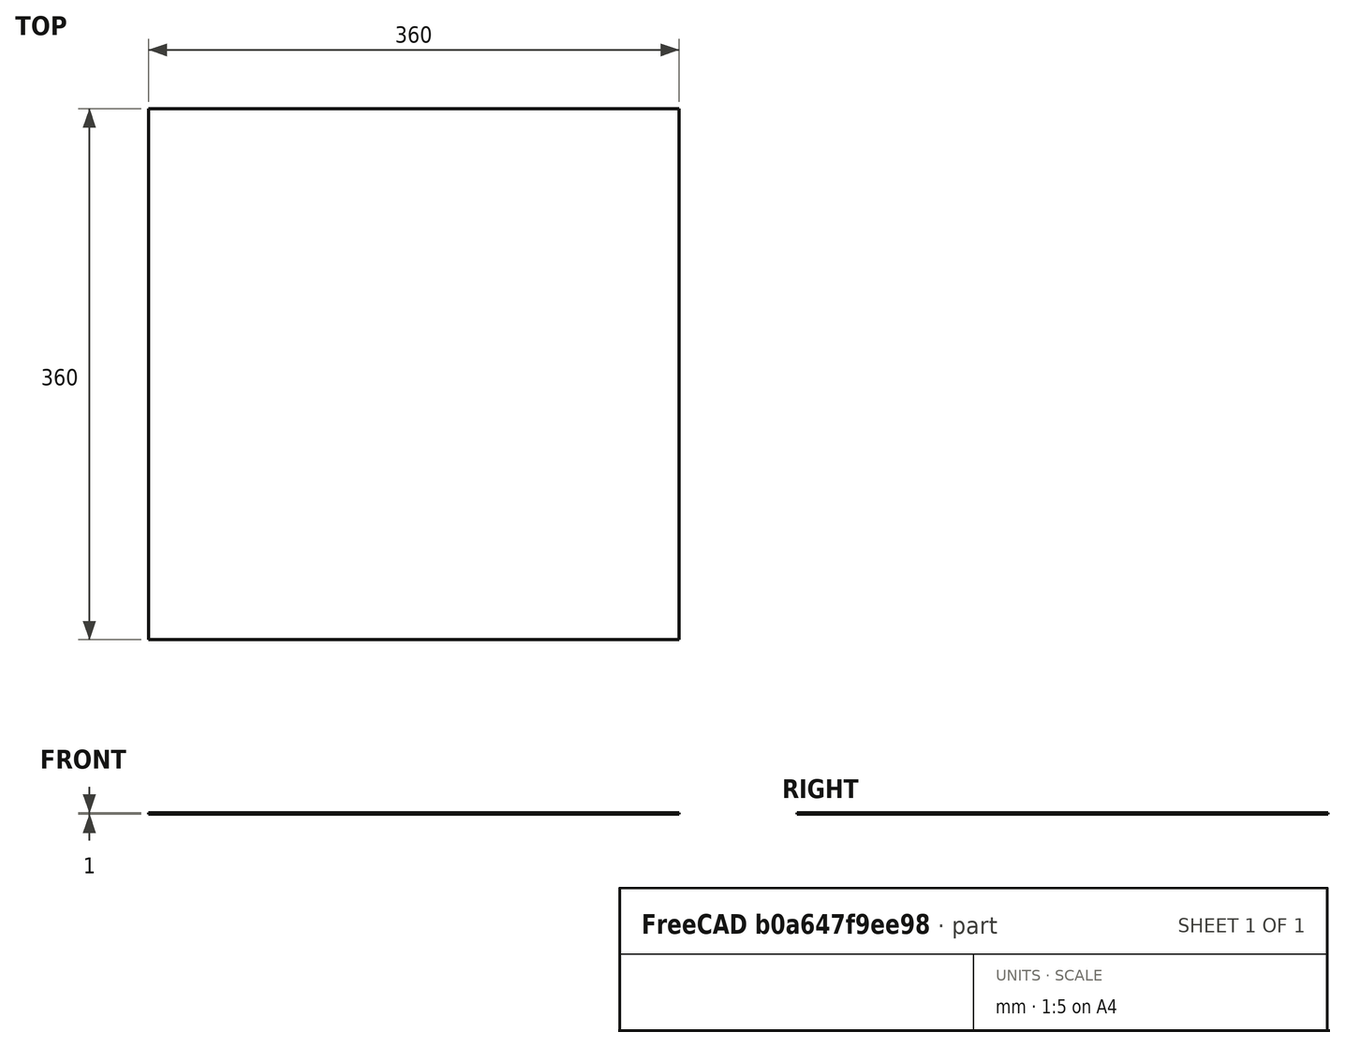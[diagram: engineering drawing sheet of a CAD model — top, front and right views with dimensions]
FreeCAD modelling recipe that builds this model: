
FCSTD DOCUMENT  (FreeCAD 0.21R33675 (Git))
Label: parabolic_simulation
License: All rights reserved
LicenseURL: http://en.wikipedia.org/wiki/All_rights_reserved
objects: Part::FeaturePython×5, App::Link×3, Part::Box×2, Spreadsheet::Sheet×1
note: 7 computed .brp shape members not serialized (recipe doc carries the construction recipe); baked Part::Feature solids carry a one-line shape summary decoded from their .brp
EXTERNAL_REF file=../../templates/tem_octagon.FCStd obj=Compound017
EXTERNAL_REF file=parabolic_screwmount.FCStd obj=Cut
EXTERNAL_REF file=parabolic_base.FCStd obj=Spreadsheet
EXTERNAL_REF file=../../sampleholder/temholder2.FCStd obj=Fusion005

FEATURE [App::Link] Link  label="TemOctagon"
  LinkedObject = -> <external ../../templates/tem_octagon.FCStd>#Compound017
FEATURE [App::Link] Link001  label="ParabolicMirrorWithScrewmount"
  LinkedObject = -> <external parabolic_screwmount.FCStd>#Cut
  expr: .Placement.Base.x = <<SimulationProperties>>.mirror_offset_x
FEATURE [Part::Box] Box  label="LowerAbsorber"
  AttacherType = Attacher::AttachEngine3D
  Height = 1
  Length = 360
  Placement = pos=(-180,-180,-41) rot=(0,0,1;0rad)
  Width = 360
FEATURE [Part::Box] Box001  label="UpperAbsorber"
  AttacherType = Attacher::AttachEngine3D
  Height = 1
  Length = 360
  Placement = pos=(-180,-180,40) rot=(0,0,1;0rad)
  Width = 360
FEATURE [Part::FeaturePython] Absorber  label="AbsorbLowerAndUpperBoundary"  # WARN: FeaturePython — macro-defined, semantics opaque (R4)
  Base = -> [Box001,Box]
  HitCoordsFromBeam = (34) [(0,0,40),(29.0617,0,40),(14.5309,25.1682,40),(-14.5309,25.1682,40),(-29.0617,3.55903e-15,40),(-14.5309,-25.1682,40),(14.5309,-25.1682,40),+27 more]
  HitCoordsFromBeamSample = (25) [(0,0,40),(-16.8699,9.73985,40),(-19.4797,2.38557e-15,40),(-16.8699,-9.73985,40),(-24.7109,20.7349,40),(-30.3124,11.0328,40),(-32.2578,3.95044e-15,40),+18 more]
  HitsFromBeam = 34
  HitsFromBeamSample = 25
  OpticalType = 1
FEATURE [Part::FeaturePython] Absorber001  label="AbsorbTemOctagon"  # WARN: FeaturePython — macro-defined, semantics opaque (R4)
  Base = -> [Link]
  HitsFromBeamSample = 0
  OpticalType = 1
FEATURE [Spreadsheet::Sheet] Spreadsheet  label="SimulationProperties"
  cells = A1='Configuration; D1='Imported from parabolic_base; G1='Calculated properties; A2='Out of focus: z; B2(outoffocus_z)=0; C2='Puts the sample out of focus by this distance; D2='Z Positon correction / Offset (downwards) ; E2(focus_offset_z)==parabolic_base#<<MirrorParameters>>.zpos_correction; G2='Sample z; H2(sample_z)==outoffocus_z - focus_offset_z; I2='The sample position; A3='Out of focus: x; B3(outoffocus_x)=0; C3='Puts the sample out of focus by this distance; G3='Sample x; H3(sample_x)==outoffocus_x; I3='The sample position; A4='Out of focus: y; B4(outoffocus_y)=0; C4='Puts the sample out of focus by this distance; G4='Sample y; H4(sample_y)==outoffocus_y; I4='The sample position; A5='Cone angle; B5(sample_cone_angle)=180; C5='The emission angle (180 deg only towards the top, 360 degree spherical); G5='Total number of rays; H5(simulation_n_rays)==raysperaxis * raysperaxis; A6='Rays per axis; B6(raysperaxis)=128; C6='Number of rays per axis; A7='Mirror position (X); B7(mirror_offset_x)=0; C7='Move the mirror this distance _away from the holder_ (negative value: Towards the holder)
FEATURE [Part::FeaturePython] Beam  label="BeamSample"  # WARN: FeaturePython — macro-defined, semantics opaque (R4)
  BeamDistance = 0.05
  BeamNrColumns = 128
  BeamNrRows = 128
  ConeAngle = 180
  HideFirstPart = false
  MaxNrReflections = 1000
  MaxRayLength = 1000000
  Order = 0
  Placement = pos=(0,0,-0.45) rot=(0,0,1;0rad)
  Power = true
  Spherical = true
  Wavelength = 400
  expr: .Placement.Base.x = <<SimulationProperties>>.sample_x
  expr: .Placement.Base.y = <<SimulationProperties>>.sample_y
  expr: .Placement.Base.z = <<SimulationProperties>>.sample_z
  expr: BeamNrColumns = <<SimulationProperties>>.raysperaxis
  expr: BeamNrRows = <<SimulationProperties>>.raysperaxis
  expr: ConeAngle = <<SimulationProperties>>.sample_cone_angle
FEATURE [Part::FeaturePython] Absorber002  label="Mirror"  # WARN: FeaturePython — macro-defined, semantics opaque (R4)
  Base = -> [Link001]
  HitsFromBeamSample = 60
  OpticalType = 0
FEATURE [App::Link] Link002  label="TemHolder"
  LinkPlacement = pos=(35.2,0,-0.48) rot=(0,1,0;-1.5708rad)
  LinkedObject = -> <external ../../sampleholder/temholder2.FCStd>#Fusion005
  Placement = pos=(35.2,0,-0.48) rot=(0,1,0;-1.5708rad)
  expr: .Placement.Base.z = -<<parabolic_base>>#<<MirrorParameters>>.step_height - 0.3
FEATURE [Part::FeaturePython] Absorber003  label="AbsorbHolder"  # WARN: FeaturePython — macro-defined, semantics opaque (R4)
  Base = -> [Link002]
  HitCoordsFromBeamSample = (77) [(1.695,0,-0.541717),(1.62634,0.477537,-0.541717),(1.42592,0.916386,-0.541717),(1.10999,1.281,-0.541717),(1.10999,-1.281,-0.541717),+72 more]
  HitsFromBeamSample = 77
  OpticalType = 1

RESOLVED EXTERNAL PARTS (link-assembly join: the EXTERNAL_REF files above that resolve inside this repo's crawl, each included once):
---- part ../../sampleholder/temholder2.FCStd = doc fcstd_919bdca02343 ----
FCSTD DOCUMENT  (FreeCAD 0.21R33675 (Git))
Label: temholder2
License: All rights reserved
LicenseURL: http://en.wikipedia.org/wiki/All_rights_reserved
objects: TechDraw::DrawViewDimension×22, Part::Cylinder×10, TechDraw::DrawProjGroupItem×10, Part::Cut×8, Part::Box×7, Part::MultiFuse×6, TechDraw::DrawSVGTemplate×2, TechDraw::DrawProjGroup×2, TechDraw::DrawPage×2, Part::MultiCommon×1
note: 32 computed .brp shape members not serialized (recipe doc carries the construction recipe); baked Part::Feature solids carry a one-line shape summary decoded from their .brp

FEATURE [Part::Cylinder] Cylinder  label="Zylinder"
  Angle = 360
  AttacherType = Attacher::AttachEngine3D
  FirstAngle = 0
  Height = 21.5
  Placement = pos=(0,0,-0.5) rot=(0,0,1;0rad)
  Radius = 2.2
  SecondAngle = 0
FEATURE [Part::Cylinder] Cylinder001  label="Zylinder001"
  Angle = 360
  AttacherType = Attacher::AttachEngine3D
  FirstAngle = 0
  Height = 18
  Placement = pos=(0,0,5) rot=(0,0,1;0rad)
  Radius = 2.5
  SecondAngle = 0
FEATURE [Part::Cylinder] Cylinder002  label="Zylinder002"
  Angle = 360
  AttacherType = Attacher::AttachEngine3D
  FirstAngle = 0
  Height = 6.2
  Placement = pos=(-3.25,0,2.95) rot=(0,1,0;1.5708rad)
  Radius = 0.75
  SecondAngle = 0
FEATURE [Part::MultiFuse] Fusion
  Shapes = -> [Cylinder,Cylinder001]
FEATURE [Part::Cut] Cut
  Base = -> Fusion
  Tool = -> Cylinder002
FEATURE [Part::Box] Box  label="Würfel"
  AttacherType = Attacher::AttachEngine3D
  Height = 27.9
  Length = 2
  Placement = pos=(-1,-5,21) rot=(0,0,1;0rad)
  Width = 10
FEATURE [Part::Cylinder] Cylinder003  label="BeamHole"
  Angle = 360
  AttacherType = Attacher::AttachEngine3D
  FirstAngle = 0
  Height = 2
  Placement = pos=(-1,0,35.2) rot=(0,1,0;1.5708rad)
  Radius = 1.1
  SecondAngle = 0
FEATURE [Part::Cylinder] Cylinder004  label="Zylinder004"
  Angle = 360
  AttacherType = Attacher::AttachEngine3D
  FirstAngle = 0
  Height = 27.4
  Placement = pos=(0,0,21.5) rot=(0,0,1;0rad)
  Radius = 3
  SecondAngle = 0
FEATURE [Part::MultiCommon] Common
  Shapes = -> [Cylinder004,Box]
FEATURE [Part::Cut] Cut001
  Base = -> Common
  Tool = -> Cylinder003
FEATURE [Part::Cylinder] Cylinder005  label="Zylinder005"
  Angle = 360
  AttacherType = Attacher::AttachEngine3D
  FirstAngle = 0
  Height = 5.5
  Placement = pos=(0,0,-0.5) rot=(0,0,1;0rad)
  Radius = 1
  SecondAngle = 0
FEATURE [Part::Cut] Cut002
  Base = -> Cut
  Tool = -> Cylinder005
FEATURE [Part::Cylinder] Cylinder006  label="ProbeHole"
  Angle = 360
  AttacherType = Attacher::AttachEngine3D
  FirstAngle = 0
  Height = 20
  Placement = pos=(-4,0,35.2) rot=(0,1,0;1.5708rad)
  Radius = 1.695
  SecondAngle = 0
FEATURE [Part::Cut] Cut003
  Base = -> Cut001
  Tool = -> Cylinder006
FEATURE [Part::Box] Box001  label="Würfel001"
  AttacherType = Attacher::AttachEngine3D
  Height = 27
  Length = 10
  Placement = pos=(1,-2.57,21) rot=(0,0,1;0rad)
  Width = 5.5
FEATURE [Part::Cut] Cut004
  Base = -> Cut003
  Tool = -> Box001
FEATURE [Part::MultiFuse] Fusion001
  Shapes = -> [Cut002,Cut004]
FEATURE [Part::Box] Box002  label="Würfel002"
  AttacherType = Attacher::AttachEngine3D
  Height = 1.5
  Length = 1
  Placement = pos=(-0.5,-3.2,21.5) rot=(0,0,1;0rad)
  Width = 6.4
FEATURE [Part::Box] Box003  label="Würfel003"
  AttacherType = Attacher::AttachEngine3D
  Height = 26
  Length = 10
  Placement = pos=(0.5,-2.19,23) rot=(0,0,1;0rad)
  Width = 4.37
FEATURE [Part::Box] Box004  label="Würfel004"
  AttacherType = Attacher::AttachEngine3D
  Height = 26
  Length = 10
  Placement = pos=(-10.5,-2.19,23) rot=(0,0,1;0rad)
  Width = 4.37
FEATURE [Part::MultiFuse] Fusion002  label="MirrorGrooves"
  Shapes = -> [Box004,Box003]
FEATURE [Part::Cut] Cut005
  Base = -> Fusion001
  Tool = -> Fusion002
FEATURE [Part::Cylinder] Cylinder007  label="M1_6__Thread1"
  Angle = 360
  AttacherType = Attacher::AttachEngine3D
  FirstAngle = 0
  Height = 50
  Placement = pos=(-4,0,31.405) rot=(0,1,0;1.5708rad)
  Radius = 0.59
  SecondAngle = 0
FEATURE [Part::Cylinder] Cylinder008  label="M1_6__Thread2"
  Angle = 360
  AttacherType = Attacher::AttachEngine3D
  FirstAngle = 0
  Height = 50
  Placement = pos=(-4,0,29.41) rot=(0,1,0;1.5708rad)
  Radius = 0.59
  SecondAngle = 0
FEATURE [Part::Box] Box005  label="Würfel005"
  AttacherType = Attacher::AttachEngine3D
  Height = 12
  Length = 10
  Placement = pos=(0.25,-2.19,36.77) rot=(0,0,1;0rad)
  Width = 4.37
FEATURE [Part::Box] Box006  label="Würfel006"
  AttacherType = Attacher::AttachEngine3D
  Height = 12
  Length = 10
  Placement = pos=(-10.25,-2.19,36.77) rot=(0,0,1;0rad)
  Width = 4.37
FEATURE [Part::MultiFuse] Fusion004
  Placement = pos=(0,0,1) rot=(0,0,1;0rad)
  Shapes = -> [Box005,Box006]
FEATURE [TechDraw::DrawSVGTemplate] Template
  EditableTexts = Designed_by_Name=Thomas Spielauer; Drawing_number=001; FC-Date=2023-05-22; FC-SC=2:1; FC-SH=2/2; FC-Title=TEM Mirror Holder; Subtitle=Version 2023-05-22
  Height = 210
  Orientation = 1
  Width = 297
FEATURE [TechDraw::DrawSVGTemplate] Template001
  EditableTexts = Designed_by_Name=Thomas Spielauer; Drawing_number=001; FC-Date=2023-05-22; FC-SC=3:2; FC-SH=2/2; FC-Title=TEM Mirror Holder; Subtitle=Version 2023-05-22
  Height = 210
  Orientation = 1
  Width = 297
FEATURE [Part::Cylinder] Cylinder009  label="M1_6__Thread3"
  Angle = 360
  AttacherType = Attacher::AttachEngine3D
  FirstAngle = 0
  Height = 50
  Placement = pos=(-4,0,27.41) rot=(0,1,0;1.5708rad)
  Radius = 0.59
  SecondAngle = 0
FEATURE [Part::MultiFuse] Fusion003  label="MirrorMountingHoles"
  Shapes = -> [Cylinder007,Cylinder008,Cylinder009]
FEATURE [Part::Cut] Cut006
  Base = -> Cut005
  Tool = -> Fusion003
FEATURE [Part::Cut] Cut007
  Base = -> Cut006
  Tool = -> Fusion004
FEATURE [Part::MultiFuse] Fusion005
  Shapes = -> [Cut007,Box002]
FEATURE [TechDraw::DrawProjGroupItem] ProjItem  label="Front"
  CoarseView = false
  Direction = (1,0,0)
  Focus = 100
  HardHidden = false
  IsoCount = 0
  IsoHidden = false
  IsoVisible = false
  LockPosition = true
  Perspective = false
  Rotation = 0
  RotationVector = (0,1,0)
  Scale = 2
  ScaleType = 2
  ScrubCount = 0
  SeamHidden = false
  SeamVisible = true
  SmoothHidden = false
  SmoothVisible = true
  Source = -> [Fusion005]
  Type = 0
  X = 0
  XDirection = (0,-2e-16,-1)
  Y = 0
FEATURE [TechDraw::DrawProjGroupItem] ProjItem001  label="Left"
  CoarseView = false
  Direction = (1e-16,2e-16,1)
  Focus = 100
  HardHidden = false
  IsoCount = 0
  IsoHidden = false
  IsoVisible = false
  LockPosition = false
  Perspective = false
  Rotation = 0
  RotationVector = (1,0,0)
  Scale = 2
  ScaleType = 2
  ScrubCount = 0
  SeamHidden = false
  SeamVisible = true
  SmoothHidden = false
  SmoothVisible = true
  Source = -> [Fusion005]
  Type = 1
  X = 54.4
  XDirection = (1,0,-1e-16)
  Y = 0
FEATURE [TechDraw::DrawProjGroupItem] ProjItem003  label="Right"
  CoarseView = false
  Direction = (1e-16,-2e-16,-1)
  Focus = 100
  HardHidden = false
  IsoCount = 0
  IsoHidden = false
  IsoVisible = false
  LockPosition = false
  Perspective = false
  Rotation = 0
  RotationVector = (1,0,0)
  Scale = 2
  ScaleType = 2
  ScrubCount = 0
  SeamHidden = false
  SeamVisible = true
  SmoothHidden = false
  SmoothVisible = true
  Source = -> [Fusion005]
  Type = 2
  X = -54.4
  XDirection = (-1,0,-1e-16)
  Y = 0
FEATURE [TechDraw::DrawProjGroupItem] ProjItem004  label="Bottom"
  CoarseView = false
  Direction = (0,-1,2e-16)
  Focus = 100
  HardHidden = false
  IsoCount = 0
  IsoHidden = false
  IsoVisible = false
  LockPosition = false
  Perspective = false
  Rotation = 0
  RotationVector = (1,0,0)
  ScaleType = 2
  ScrubCount = 0
  SeamHidden = false
  SeamVisible = true
  SmoothHidden = false
  SmoothVisible = true
  Source = -> [Fusion005]
  Type = 5
  X = 0
  XDirection = (0,-2e-16,-1)
  Y = 41.4
FEATURE [TechDraw::DrawProjGroup] ProjGroup
  Anchor = -> ProjItem
  AutoDistribute = true
  LockPosition = false
  ProjectionType = 0
  Rotation = 0
  Scale = 2
  ScaleType = 1
  Source = -> [Fusion005]
  Views = -> [ProjItem,ProjItem001,ProjItem003,ProjItem004]
  X = 148.5
  Y = 105
  spacingX = 0
  spacingY = 30
FEATURE [TechDraw::DrawViewDimension] Dimension
  AngleOverride = false
  Arbitrary = false
  ArbitraryTolerances = false
  EqualTolerance = true
  ExtensionAngle = 0
  FormatSpec = %.2w
  FormatSpecOverTolerance = %+.2w
  FormatSpecUnderTolerance = %+.2w
  Inverted = false
  LineAngle = 0
  LockPosition = false
  MeasureType = 1
  OverTolerance = 0
  References2D = -> [ProjItem004]
  Rotation = 0
  ScaleType = 0
  TheoreticalExact = false
  Type = 0
  UnderTolerance = 0
  X = -0.570385
  Y = 36.7256
FEATURE [TechDraw::DrawViewDimension] Dimension001
  AngleOverride = false
  Arbitrary = false
  ArbitraryTolerances = false
  EqualTolerance = true
  ExtensionAngle = 0
  FormatSpec = %.2w
  FormatSpecOverTolerance = %+.2w
  FormatSpecUnderTolerance = %+.2w
  Inverted = false
  LineAngle = 0
  LockPosition = false
  MeasureType = 1
  OverTolerance = 0
  References2D = -> [ProjItem004]
  Rotation = 0
  ScaleType = 0
  TheoreticalExact = false
  Type = 0
  UnderTolerance = 0
  X = 43.2488
  Y = 27.3992
FEATURE [TechDraw::DrawViewDimension] Dimension002
  AngleOverride = false
  Arbitrary = false
  ArbitraryTolerances = false
  EqualTolerance = true
  ExtensionAngle = 0
  FormatSpec = %.2w
  FormatSpecOverTolerance = %+.2w
  FormatSpecUnderTolerance = %+.2w
  Inverted = false
  LineAngle = 0
  LockPosition = false
  MeasureType = 1
  OverTolerance = 0
  References2D = -> [ProjItem004]
  Rotation = 0
  ScaleType = 0
  TheoreticalExact = false
  Type = 0
  UnderTolerance = 0
  X = 20.4028
  Y = 27.4177
FEATURE [TechDraw::DrawViewDimension] Dimension003
  AngleOverride = false
  Arbitrary = false
  ArbitraryTolerances = false
  EqualTolerance = true
  ExtensionAngle = 0
  FormatSpec = %.2w
  FormatSpecOverTolerance = %+.2w
  FormatSpecUnderTolerance = %+.2w
  Inverted = false
  LineAngle = 0
  LockPosition = false
  MeasureType = 1
  OverTolerance = 0
  References2D = -> [ProjItem004]
  Rotation = 0
  ScaleType = 0
  TheoreticalExact = false
  Type = 0
  UnderTolerance = 0
  X = -20.5047
  Y = 16.0274
FEATURE [TechDraw::DrawViewDimension] Dimension004
  AngleOverride = false
  Arbitrary = false
  ArbitraryTolerances = false
  EqualTolerance = true
  ExtensionAngle = 0
  FormatSpec = %.2w
  FormatSpecOverTolerance = %+.2w
  FormatSpecUnderTolerance = %+.2w
  Inverted = false
  LineAngle = 0
  LockPosition = false
  MeasureType = 1
  OverTolerance = 0
  References2D = -> [ProjItem004]
  Rotation = 0
  ScaleType = 0
  TheoreticalExact = false
  Type = 0
  UnderTolerance = 0
  X = 8.18137
  Y = 19.112
FEATURE [TechDraw::DrawViewDimension] Dimension005
  AngleOverride = false
  Arbitrary = false
  ArbitraryTolerances = false
  EqualTolerance = true
  ExtensionAngle = 0
  FormatSpec = %.2w
  FormatSpecOverTolerance = %+.2w
  FormatSpecUnderTolerance = %+.2w
  Inverted = false
  LineAngle = 0
  LockPosition = false
  MeasureType = 1
  OverTolerance = 0
  References2D = -> [ProjItem004]
  Rotation = 0
  ScaleType = 0
  TheoreticalExact = false
  Type = 0
  UnderTolerance = 0
  X = 68.2961
  Y = 3.13583
FEATURE [TechDraw::DrawViewDimension] Dimension006
  AngleOverride = false
  Arbitrary = false
  ArbitraryTolerances = false
  EqualTolerance = true
  ExtensionAngle = 0
  FormatSpec = %.2w
  FormatSpecOverTolerance = %+.2w
  FormatSpecUnderTolerance = %+.2w
  Inverted = false
  LineAngle = 0
  LockPosition = false
  MeasureType = 1
  OverTolerance = 0
  References2D = -> [ProjItem004]
  Rotation = 0
  ScaleType = 0
  TheoreticalExact = false
  Type = 0
  UnderTolerance = 0
  X = 78.1774
  Y = 10.4092
FEATURE [TechDraw::DrawViewDimension] Dimension007
  AngleOverride = false
  Arbitrary = false
  ArbitraryTolerances = false
  EqualTolerance = true
  ExtensionAngle = 0
  FormatSpec = %.2w
  FormatSpecOverTolerance = %+.2w
  FormatSpecUnderTolerance = %+.2w
  Inverted = false
  LineAngle = 0
  LockPosition = false
  MeasureType = 1
  OverTolerance = 0
  References2D = -> [ProjItem004]
  Rotation = 0
  ScaleType = 0
  TheoreticalExact = false
  Type = 0
  UnderTolerance = 0
  X = -59.0159
  Y = 3.08043
FEATURE [TechDraw::DrawViewDimension] Dimension008
  AngleOverride = false
  Arbitrary = false
  ArbitraryTolerances = false
  EqualTolerance = true
  ExtensionAngle = 0
  FormatSpec = %.2w
  FormatSpecOverTolerance = %+.2w
  FormatSpecUnderTolerance = %+.2w
  Inverted = false
  LineAngle = 0
  LockPosition = false
  MeasureType = 1
  OverTolerance = 0
  References2D = -> [ProjItem004]
  Rotation = 0
  ScaleType = 0
  TheoreticalExact = false
  Type = 0
  UnderTolerance = 0
  X = 17.8117
  Y = -5.66689
FEATURE [TechDraw::DrawViewDimension] Dimension010
  AngleOverride = false
  Arbitrary = false
  ArbitraryTolerances = false
  EqualTolerance = true
  ExtensionAngle = 0
  FormatSpec = %.2w
  FormatSpecOverTolerance = %+.2w
  FormatSpecUnderTolerance = %+.2w
  Inverted = false
  LineAngle = 0
  LockPosition = false
  MeasureType = 1
  OverTolerance = 0
  References2D = -> [ProjItem]
  Rotation = 0
  ScaleType = 0
  TheoreticalExact = false
  Type = 0
  UnderTolerance = 0
  X = -80.5776
  Y = 1.58527
FEATURE [TechDraw::DrawViewDimension] Dimension011
  AngleOverride = false
  Arbitrary = false
  ArbitraryTolerances = false
  EqualTolerance = true
  ExtensionAngle = 0
  FormatSpec = %.2w
  FormatSpecOverTolerance = %+.2w
  FormatSpecUnderTolerance = %+.2w
  Inverted = false
  LineAngle = 0
  LockPosition = false
  MeasureType = 1
  OverTolerance = 0
  References2D = -> [ProjItem]
  Rotation = 0
  ScaleType = 0
  TheoreticalExact = false
  Type = 0
  UnderTolerance = 0
  X = -69.6018
  Y = 1.50597
FEATURE [TechDraw::DrawViewDimension] Dimension012
  AngleOverride = false
  Arbitrary = false
  ArbitraryTolerances = false
  EqualTolerance = true
  ExtensionAngle = 0
  FormatSpec = %.2w
  FormatSpecOverTolerance = %+.2w
  FormatSpecUnderTolerance = %+.2w
  Inverted = false
  LineAngle = 0
  LockPosition = false
  MeasureType = 1
  OverTolerance = 0
  References2D = -> [ProjItem]
  Rotation = 0
  ScaleType = 0
  TheoreticalExact = false
  Type = 0
  UnderTolerance = 0
  X = 80.5725
  Y = 4.77787
FEATURE [TechDraw::DrawViewDimension] Dimension013
  AngleOverride = false
  Arbitrary = false
  ArbitraryTolerances = false
  EqualTolerance = true
  ExtensionAngle = 0
  FormatSpec = %.2w
  FormatSpecOverTolerance = %+.2w
  FormatSpecUnderTolerance = %+.2w
  Inverted = false
  LineAngle = 0
  LockPosition = false
  MeasureType = 1
  OverTolerance = 0
  References2D = -> [ProjItem]
  Rotation = 0
  ScaleType = 0
  TheoreticalExact = false
  Type = 0
  UnderTolerance = 0
  X = 58.3431
  Y = 1.78358
FEATURE [TechDraw::DrawViewDimension] Dimension014
  AngleOverride = false
  Arbitrary = false
  ArbitraryTolerances = false
  EqualTolerance = true
  ExtensionAngle = 0
  FormatSpec = %.2w
  FormatSpecOverTolerance = %+.2w
  FormatSpecUnderTolerance = %+.2w
  Inverted = false
  LineAngle = 0
  LockPosition = false
  MeasureType = 1
  OverTolerance = 0
  References2D = -> [ProjItem]
  Rotation = 0
  ScaleType = 0
  TheoreticalExact = false
  Type = 0
  UnderTolerance = 0
  X = 69.2835
  Y = 2.85821
FEATURE [TechDraw::DrawViewDimension] Dimension015
  AngleOverride = false
  Arbitrary = false
  ArbitraryTolerances = false
  EqualTolerance = true
  ExtensionAngle = 0
  FormatSpec = ⌀%.2w
  FormatSpecOverTolerance = %+.2w
  FormatSpecUnderTolerance = %+.2w
  Inverted = false
  LineAngle = 0
  LockPosition = false
  MeasureType = 1
  OverTolerance = 0
  References2D = -> [ProjItem]
  Rotation = 0
  ScaleType = 0
  TheoreticalExact = false
  Type = 5
  UnderTolerance = 0
  X = -17.8818
  Y = -30.5126
FEATURE [TechDraw::DrawViewDimension] Dimension016
  AngleOverride = false
  Arbitrary = false
  ArbitraryTolerances = false
  EqualTolerance = true
  ExtensionAngle = 0
  FormatSpec = ⌀%.2w
  FormatSpecOverTolerance = %+.2w
  FormatSpecUnderTolerance = %+.2w
  Inverted = false
  LineAngle = 0
  LockPosition = false
  MeasureType = 1
  OverTolerance = 0
  References2D = -> [ProjItem]
  Rotation = 0
  ScaleType = 0
  TheoreticalExact = false
  Type = 5
  UnderTolerance = 0
  X = -6.5506
  Y = -20.9661
FEATURE [TechDraw::DrawViewDimension] Dimension017
  AngleOverride = false
  Arbitrary = false
  ArbitraryTolerances = false
  EqualTolerance = true
  ExtensionAngle = 0
  FormatSpec = ⌀%.2w
  FormatSpecOverTolerance = %+.2w
  FormatSpecUnderTolerance = %+.2w
  Inverted = false
  LineAngle = 0
  LockPosition = false
  MeasureType = 1
  OverTolerance = 0
  References2D = -> [ProjItem]
  Rotation = 0
  ScaleType = 0
  TheoreticalExact = false
  Type = 5
  UnderTolerance = 0
  X = 0
  Y = -20.3856
FEATURE [TechDraw::DrawViewDimension] Dimension018
  AngleOverride = false
  Arbitrary = false
  ArbitraryTolerances = false
  EqualTolerance = true
  ExtensionAngle = 0
  FormatSpec = %.2w
  FormatSpecOverTolerance = %+.2w
  FormatSpecUnderTolerance = %+.2w
  Inverted = false
  LineAngle = 0
  LockPosition = false
  MeasureType = 1
  OverTolerance = 0
  References2D = -> [ProjItem]
  Rotation = 0
  ScaleType = 0
  TheoreticalExact = false
  Type = 0
  UnderTolerance = 0
  X = 37.2627
  Y = -7.40421
FEATURE [TechDraw::DrawViewDimension] Dimension019
  AngleOverride = false
  Arbitrary = false
  ArbitraryTolerances = false
  EqualTolerance = true
  ExtensionAngle = 0
  FormatSpec = %.2w
  FormatSpecOverTolerance = %+.2w
  FormatSpecUnderTolerance = %+.2w
  Inverted = false
  LineAngle = 0
  LockPosition = false
  MeasureType = 1
  OverTolerance = 0
  References2D = -> [ProjItem001]
  Rotation = 0
  ScaleType = 0
  TheoreticalExact = false
  Type = 0
  UnderTolerance = 0
  X = 14.265
  Y = 2.24769
FEATURE [TechDraw::DrawViewDimension] Dimension020
  AngleOverride = false
  Arbitrary = false
  ArbitraryTolerances = false
  EqualTolerance = true
  ExtensionAngle = 0
  FormatSpec = ⌀%.2w
  FormatSpecOverTolerance = %+.2w
  FormatSpecUnderTolerance = %+.2w
  Inverted = false
  LineAngle = 0
  LockPosition = false
  MeasureType = 1
  OverTolerance = 0
  References2D = -> [ProjItem001]
  Rotation = 0
  ScaleType = 0
  TheoreticalExact = false
  Type = 5
  UnderTolerance = 0
  X = -8.46963
  Y = -24.8974
FEATURE [TechDraw::DrawViewDimension] Dimension021
  AngleOverride = false
  Arbitrary = false
  ArbitraryTolerances = false
  EqualTolerance = true
  ExtensionAngle = 0
  FormatSpec = %.2w
  FormatSpecOverTolerance = %+.2w
  FormatSpecUnderTolerance = %+.2w
  Inverted = false
  LineAngle = 0
  LockPosition = false
  MeasureType = 1
  OverTolerance = 0
  References2D = -> [ProjItem003]
  Rotation = 0
  ScaleType = 0
  TheoreticalExact = false
  Type = 0
  UnderTolerance = 0
  X = 0
  Y = 15.8224
FEATURE [TechDraw::DrawViewDimension] Dimension022
  AngleOverride = false
  Arbitrary = false
  ArbitraryTolerances = false
  EqualTolerance = true
  ExtensionAngle = 0
  FormatSpec = %.2w
  FormatSpecOverTolerance = %+.2w
  FormatSpecUnderTolerance = %+.2w
  Inverted = false
  LineAngle = 0
  LockPosition = false
  MeasureType = 1
  OverTolerance = 0
  References2D = -> [ProjItem003]
  Rotation = 0
  ScaleType = 0
  TheoreticalExact = false
  Type = 0
  UnderTolerance = 0
  X = -0.516427
  Y = -17.6903
FEATURE [TechDraw::DrawPage] Page
  KeepUpdated = true
  NextBalloonIndex = 1
  ProjectionType = 0
  Template = -> Template
  Views = -> [ProjGroup,Dimension,Dimension001,Dimension002,Dimension003,Dimension004,Dimension005,Dimension006,Dimension007,Dimension008,Dimension010,Dimension011,Dimension012,Dimension013,Dimension014,Dimension015,Dimension016,Dimension017,Dimension018,Dimension019,Dimension020,Dimension021,Dimension022]
FEATURE [TechDraw::DrawProjGroupItem] ProjItem005  label="Front001"
  CoarseView = false
  Direction = (0.582,-0.433,-0.688)
  Focus = 100
  HardHidden = false
  IsoCount = 0
  IsoHidden = false
  IsoVisible = false
  LockPosition = true
  Perspective = false
  Rotation = 0
  RotationVector = (-0.012,0.841,-0.54)
  Scale = 1.5
  ScaleType = 2
  ScrubCount = 0
  SeamHidden = false
  SeamVisible = true
  SmoothHidden = false
  SmoothVisible = true
  Source = -> [Fusion005]
  Type = 0
  X = 0
  XDirection = (-0.012,0.841,-0.54)
  Y = 0
FEATURE [TechDraw::DrawProjGroupItem] ProjItem006  label="FrontBottomRight"
  CoarseView = false
  Direction = (-0.140356,0.0494879,-0.988863)
  Focus = 100
  HardHidden = false
  IsoCount = 0
  IsoHidden = false
  IsoVisible = false
  LockPosition = false
  Perspective = false
  Rotation = 0
  RotationVector = (1,0,0)
  Scale = 1.5
  ScaleType = 2
  ScrubCount = 0
  SeamHidden = false
  SeamVisible = true
  SmoothHidden = false
  SmoothVisible = true
  Source = -> [Fusion005]
  Type = 9
  X = -51.338
  XDirection = (-0.420275,0.901329,0.10476)
  Y = 48.7411
FEATURE [TechDraw::DrawProjGroupItem] ProjItem007  label="FrontBottomLeft"
  CoarseView = false
  Direction = (-0.126236,-0.922281,-0.365326)
  Focus = 100
  HardHidden = false
  IsoCount = 0
  IsoHidden = false
  IsoVisible = false
  LockPosition = false
  Perspective = false
  Rotation = 0
  RotationVector = (1,0,0)
  Scale = 1.5
  ScaleType = 2
  ScrubCount = 0
  SeamHidden = false
  SeamVisible = true
  SmoothHidden = false
  SmoothVisible = true
  Source = -> [Fusion005]
  Type = 8
  X = 57.198
  XDirection = (0.40298,0.288839,-0.868435)
  Y = 48.7411
FEATURE [TechDraw::DrawProjGroupItem] ProjItem008  label="Left001"
  CoarseView = false
  Direction = (0.012229,-0.841576,0.54)
  Focus = 100
  HardHidden = false
  IsoCount = 0
  IsoHidden = false
  IsoVisible = false
  LockPosition = false
  Perspective = false
  Rotation = 0
  RotationVector = (1,0,0)
  Scale = 1.5
  ScaleType = 2
  ScrubCount = 0
  SeamHidden = false
  SeamVisible = true
  SmoothHidden = false
  SmoothVisible = true
  Source = -> [Fusion005]
  Type = 1
  X = 57.198
  XDirection = (0.582129,-0.433096,-0.688152)
  Y = 0
FEATURE [TechDraw::DrawProjGroupItem] ProjItem009  label="Right001"
  CoarseView = false
  Direction = (-0.012229,0.841576,-0.54)
  Focus = 100
  HardHidden = false
  IsoCount = 0
  IsoHidden = false
  IsoVisible = false
  LockPosition = false
  Perspective = false
  Rotation = 0
  RotationVector = (1,0,0)
  Scale = 1.5
  ScaleType = 2
  ScrubCount = 0
  SeamHidden = false
  SeamVisible = true
  SmoothHidden = false
  SmoothVisible = true
  Source = -> [Fusion005]
  Type = 2
  X = -51.338
  XDirection = (-0.582129,0.433096,0.688152)
  Y = 0
FEATURE [TechDraw::DrawProjGroupItem] ProjItem010  label="Bottom001"
  CoarseView = false
  Direction = (-0.813005,-0.322765,-0.48461)
  Focus = 100
  HardHidden = false
  IsoCount = 0
  IsoHidden = false
  IsoVisible = false
  LockPosition = false
  Perspective = false
  Rotation = 0
  RotationVector = (1,0,0)
  Scale = 1.5
  ScaleType = 2
  ScrubCount = 0
  SeamHidden = false
  SeamVisible = true
  SmoothHidden = false
  SmoothVisible = true
  Source = -> [Fusion005]
  Type = 5
  X = 0
  XDirection = (-0.012229,0.841576,-0.54)
  Y = 48.7411
FEATURE [TechDraw::DrawProjGroup] ProjGroup001
  Anchor = -> ProjItem005
  AutoDistribute = true
  LockPosition = false
  ProjectionType = 0
  Rotation = 0
  Scale = 1.5
  ScaleType = 2
  Source = -> [Fusion005]
  Views = -> [ProjItem005,ProjItem006,ProjItem007,ProjItem008,ProjItem009,ProjItem010]
  X = 148.5
  Y = 105
  spacingX = 0
  spacingY = 0
FEATURE [TechDraw::DrawPage] Page001
  KeepUpdated = true
  NextBalloonIndex = 1
  ProjectionType = 0
  Template = -> Template001
  Views = -> [ProjGroup001]
---- part ../../templates/tem_octagon.FCStd = doc fcstd_6cc3e1e13852 ----
FCSTD DOCUMENT  (FreeCAD 0.20R29603 (Git))
Label: tem_octagon
License: All rights reserved
LicenseURL: http://en.wikipedia.org/wiki/All_rights_reserved
objects: Part::Compound×18, Part::Cylinder×16, Part::Cut×10, Part::Feature×8, Part::FeaturePython×8, Part::Part2DObjectPython×2, Part::Extrusion×2
note: 64 computed .brp shape members not serialized (recipe doc carries the construction recipe); baked Part::Feature solids carry a one-line shape summary decoded from their .brp

FEATURE [Part::Part2DObjectPython] Wire  # Draft 2D object (typed FeaturePython)
  Area = 106458
  ChamferSize = 0
  Closed = true
  End = (74.24,179.24,-40)
  FilletRadius = 0
  Length = 1187.89
  MakeFace = true
  Placement = pos=(0,0,-40) rot=(0,0,1;0rad)
  Points = (9) [(74.24,179.24,-2.13163e-14),(179.24,74.24,0),(179.24,-74.24,0),(74.24,-179.24,0),(-74.24,-179.24,0),(-179.24,-74.24,0),(-179.24,74.24,0),(-74.24,179.24,0),(74.24,179.24,-2.13163e-14)]
  Start = (74.24,179.24,-40)
  Subdivisions = 0
FEATURE [Part::Extrusion] Extrude
  Base = -> Wire
  Dir = (0,0,1)
  DirMode = 2
  FaceMakerClass = Part::FaceMakerBullseye
  LengthFwd = 80
  LengthRev = 0
  Solid = false
  Symmetric = false
FEATURE [Part::Part2DObjectPython] Wire001  # Draft 2D object (typed FeaturePython)
  Area = 85639.1
  ChamferSize = 0
  Closed = true
  End = (66.59,160.76,-40)
  FilletRadius = 0
  Length = 1065.43
  MakeFace = true
  Placement = pos=(0,0,-40) rot=(0,0,1;0rad)
  Points = (9) [(66.59,160.76,0),(160.76,66.59,0),(160.76,-66.59,0),(66.59,-160.76,0),(-66.59,-160.76,0),(-160.76,-66.59,0),(-160.76,66.59,0),(-66.59,160.76,0),(66.59,160.76,0)]
  Start = (66.59,160.76,-40)
  Subdivisions = 0
FEATURE [Part::Extrusion] Extrude001
  Base = -> Wire001
  Dir = (0,0,1)
  DirMode = 2
  FaceMakerClass = Part::FaceMakerBullseye
  LengthFwd = 80
  LengthRev = 0
  Solid = false
  Symmetric = false
FEATURE [Part::Cut] Cut
  Base = -> Extrude
  Tool = -> Extrude001
FEATURE [Part::Feature] Solid  label="Hositrad_CF35-Blank"
  Placement = pos=(0,166.75,0) rot=(0,0,1;0rad)
  shape: bbox 70 x 12.7 x 70 mm, 58 faces (baked)
FEATURE [Part::Cylinder] Cylinder  label="Zylinder"
  Angle = 360
  AttacherType = Attacher::AttachEngine3D
  FirstAngle = 0
  Height = 20
  Placement = pos=(0,179.75,0) rot=(1,0,0;1.5708rad)
  Radius = 34.5
  SecondAngle = 0
FEATURE [Part::Cylinder] Cylinder001  label="Zylinder001"
  Angle = 360
  AttacherType = Attacher::AttachEngine3D
  FirstAngle = 0
  Height = 20
  Placement = pos=(0,179.75,0) rot=(1,0,0;1.5708rad)
  Radius = 22.25
  SecondAngle = 0
FEATURE [Part::Cylinder] Cylinder002  label="Zylinder002"
  Angle = 360
  AttacherType = Attacher::AttachEngine3D
  FirstAngle = 0
  Height = 20
  Placement = pos=(0,179.75,0) rot=(1,0,0;1.5708rad)
  Radius = 34.5
  SecondAngle = 0
FEATURE [Part::Compound] Compound
  Links = -> [Cylinder002]
  Placement = pos=(0,0,0) rot=(0,0,1;0.785398rad)
FEATURE [Part::Cylinder] Cylinder003  label="Zylinder003"
  Angle = 360
  AttacherType = Attacher::AttachEngine3D
  FirstAngle = 0
  Height = 20
  Placement = pos=(0,179.75,0) rot=(1,0,0;1.5708rad)
  Radius = 34.5
  SecondAngle = 0
FEATURE [Part::Compound] Compound001
  Links = -> [Cylinder003]
  Placement = pos=(0,0,0) rot=(0,0,1;1.5708rad)
FEATURE [Part::Cylinder] Cylinder004  label="Zylinder004"
  Angle = 360
  AttacherType = Attacher::AttachEngine3D
  FirstAngle = 0
  Height = 20
  Placement = pos=(0,179.75,0) rot=(1,0,0;1.5708rad)
  Radius = 34.5
  SecondAngle = 0
FEATURE [Part::Compound] Compound002
  Links = -> [Cylinder004]
  Placement = pos=(0,0,0) rot=(0,0,1;2.35619rad)
FEATURE [Part::Cylinder] Cylinder005  label="Zylinder005"
  Angle = 360
  AttacherType = Attacher::AttachEngine3D
  FirstAngle = 0
  Height = 20
  Placement = pos=(0,179.75,0) rot=(1,0,0;1.5708rad)
  Radius = 34.5
  SecondAngle = 0
FEATURE [Part::Compound] Compound003
  Links = -> [Cylinder005]
  Placement = pos=(0,0,0) rot=(0,0,1;3.14159rad)
FEATURE [Part::Cylinder] Cylinder006  label="Zylinder006"
  Angle = 360
  AttacherType = Attacher::AttachEngine3D
  FirstAngle = 0
  Height = 20
  Placement = pos=(0,179.75,0) rot=(1,0,0;1.5708rad)
  Radius = 34.5
  SecondAngle = 0
FEATURE [Part::Compound] Compound004
  Links = -> [Cylinder006]
  Placement = pos=(0,0,0) rot=(0,0,1;3.92699rad)
FEATURE [Part::Cylinder] Cylinder007  label="Zylinder007"
  Angle = 360
  AttacherType = Attacher::AttachEngine3D
  FirstAngle = 0
  Height = 20
  Placement = pos=(0,179.75,0) rot=(1,0,0;1.5708rad)
  Radius = 34.5
  SecondAngle = 0
FEATURE [Part::Compound] Compound005
  Links = -> [Cylinder007]
  Placement = pos=(0,0,0) rot=(0,0,1;4.71239rad)
FEATURE [Part::Cylinder] Cylinder008  label="Zylinder008"
  Angle = 360
  AttacherType = Attacher::AttachEngine3D
  FirstAngle = 0
  Height = 20
  Placement = pos=(0,179.75,0) rot=(1,0,0;1.5708rad)
  Radius = 34.5
  SecondAngle = 0
FEATURE [Part::Compound] Compound006
  Links = -> [Cylinder008]
  Placement = pos=(0,0,0) rot=(0,0,1;5.49779rad)
FEATURE [Part::Compound] Compound007
  Links = -> [Cylinder,Compound,Compound001,Compound002,Compound003,Compound004,Compound005,Compound006]
FEATURE [Part::Cut] Cut001
  Base = -> Cut
  Tool = -> Compound007
FEATURE [Part::Cut] Cut002
  Base = -> Solid
  Tool = -> Cylinder001
FEATURE [Part::FeaturePython] Tube  # WARN: FeaturePython — macro-defined, semantics opaque (R4)
  AttacherType = Attacher::AttachEngine3D
  Height = 6
  InnerRadius = 22.25
  OuterRadius = 34.5
  Placement = pos=(0,166.76,0) rot=(1,0,0;1.5708rad)
FEATURE [Part::Compound] Compound008
  Links = -> [Tube,Cut002]
FEATURE [Part::Cylinder] Cylinder009  label="Zylinder009"
  Angle = 360
  AttacherType = Attacher::AttachEngine3D
  FirstAngle = 0
  Height = 20
  Placement = pos=(0,179.75,0) rot=(1,0,0;1.5708rad)
  Radius = 22.25
  SecondAngle = 0
FEATURE [Part::Feature] Solid001  label="Hositrad_CF35-Blank001"
  Placement = pos=(0,166.75,0) rot=(0,0,1;0rad)
  shape: bbox 70 x 12.7 x 70 mm, 58 faces (baked)
FEATURE [Part::Cut] Cut003
  Base = -> Solid001
  Tool = -> Cylinder009
FEATURE [Part::FeaturePython] Tube001  # WARN: FeaturePython — macro-defined, semantics opaque (R4)
  AttacherType = Attacher::AttachEngine3D
  Height = 6
  InnerRadius = 22.25
  OuterRadius = 34.5
  Placement = pos=(0,166.76,0) rot=(1,0,0;1.5708rad)
FEATURE [Part::Compound] Compound009
  Links = -> [Tube001,Cut003]
  Placement = pos=(0,0,0) rot=(0,0,1;0.785398rad)
FEATURE [Part::Cylinder] Cylinder010  label="Zylinder010"
  Angle = 360
  AttacherType = Attacher::AttachEngine3D
  FirstAngle = 0
  Height = 20
  Placement = pos=(0,179.75,0) rot=(1,0,0;1.5708rad)
  Radius = 22.25
  SecondAngle = 0
FEATURE [Part::Feature] Solid002  label="Hositrad_CF35-Blank002"
  Placement = pos=(0,166.75,0) rot=(0,0,1;0rad)
  shape: bbox 70 x 12.7 x 70 mm, 58 faces (baked)
FEATURE [Part::Cut] Cut004
  Base = -> Solid002
  Tool = -> Cylinder010
FEATURE [Part::FeaturePython] Tube002  # WARN: FeaturePython — macro-defined, semantics opaque (R4)
  AttacherType = Attacher::AttachEngine3D
  Height = 6
  InnerRadius = 22.25
  OuterRadius = 34.5
  Placement = pos=(0,166.76,0) rot=(1,0,0;1.5708rad)
FEATURE [Part::Compound] Compound010
  Links = -> [Tube002,Cut004]
  Placement = pos=(0,0,0) rot=(0,0,1;1.5708rad)
FEATURE [Part::Cylinder] Cylinder011  label="Zylinder011"
  Angle = 360
  AttacherType = Attacher::AttachEngine3D
  FirstAngle = 0
  Height = 20
  Placement = pos=(0,179.75,0) rot=(1,0,0;1.5708rad)
  Radius = 22.25
  SecondAngle = 0
FEATURE [Part::Feature] Solid003  label="Hositrad_CF35-Blank003"
  Placement = pos=(0,166.75,0) rot=(0,0,1;0rad)
  shape: bbox 70 x 12.7 x 70 mm, 58 faces (baked)
FEATURE [Part::Cut] Cut005
  Base = -> Solid003
  Tool = -> Cylinder011
FEATURE [Part::FeaturePython] Tube003  # WARN: FeaturePython — macro-defined, semantics opaque (R4)
  AttacherType = Attacher::AttachEngine3D
  Height = 6
  InnerRadius = 22.25
  OuterRadius = 34.5
  Placement = pos=(0,166.76,0) rot=(1,0,0;1.5708rad)
FEATURE [Part::Compound] Compound011
  Links = -> [Tube003,Cut005]
  Placement = pos=(0,0,0) rot=(0,0,1;2.35619rad)
FEATURE [Part::Cylinder] Cylinder012  label="Zylinder012"
  Angle = 360
  AttacherType = Attacher::AttachEngine3D
  FirstAngle = 0
  Height = 20
  Placement = pos=(0,179.75,0) rot=(1,0,0;1.5708rad)
  Radius = 22.25
  SecondAngle = 0
FEATURE [Part::Feature] Solid004  label="Hositrad_CF35-Blank004"
  Placement = pos=(0,166.75,0) rot=(0,0,1;0rad)
  shape: bbox 70 x 12.7 x 70 mm, 58 faces (baked)
FEATURE [Part::Cut] Cut006
  Base = -> Solid004
  Tool = -> Cylinder012
FEATURE [Part::FeaturePython] Tube004  # WARN: FeaturePython — macro-defined, semantics opaque (R4)
  AttacherType = Attacher::AttachEngine3D
  Height = 6
  InnerRadius = 22.25
  OuterRadius = 34.5
  Placement = pos=(0,166.76,0) rot=(1,0,0;1.5708rad)
FEATURE [Part::Compound] Compound012
  Links = -> [Tube004,Cut006]
  Placement = pos=(0,0,0) rot=(0,0,1;3.14159rad)
FEATURE [Part::Cylinder] Cylinder013  label="Zylinder013"
  Angle = 360
  AttacherType = Attacher::AttachEngine3D
  FirstAngle = 0
  Height = 20
  Placement = pos=(0,179.75,0) rot=(1,0,0;1.5708rad)
  Radius = 22.25
  SecondAngle = 0
FEATURE [Part::Feature] Solid005  label="Hositrad_CF35-Blank005"
  Placement = pos=(0,166.75,0) rot=(0,0,1;0rad)
  shape: bbox 70 x 12.7 x 70 mm, 58 faces (baked)
FEATURE [Part::Cut] Cut007
  Base = -> Solid005
  Tool = -> Cylinder013
FEATURE [Part::FeaturePython] Tube005  # WARN: FeaturePython — macro-defined, semantics opaque (R4)
  AttacherType = Attacher::AttachEngine3D
  Height = 6
  InnerRadius = 22.25
  OuterRadius = 34.5
  Placement = pos=(0,166.76,0) rot=(1,0,0;1.5708rad)
FEATURE [Part::Compound] Compound013
  Links = -> [Tube005,Cut007]
  Placement = pos=(0,0,0) rot=(0,0,1;3.92699rad)
FEATURE [Part::Cylinder] Cylinder014  label="Zylinder014"
  Angle = 360
  AttacherType = Attacher::AttachEngine3D
  FirstAngle = 0
  Height = 20
  Placement = pos=(0,179.75,0) rot=(1,0,0;1.5708rad)
  Radius = 22.25
  SecondAngle = 0
FEATURE [Part::Feature] Solid006  label="Hositrad_CF35-Blank006"
  Placement = pos=(0,166.75,0) rot=(0,0,1;0rad)
  shape: bbox 70 x 12.7 x 70 mm, 58 faces (baked)
FEATURE [Part::Cut] Cut008
  Base = -> Solid006
  Tool = -> Cylinder014
FEATURE [Part::FeaturePython] Tube006  # WARN: FeaturePython — macro-defined, semantics opaque (R4)
  AttacherType = Attacher::AttachEngine3D
  Height = 6
  InnerRadius = 22.25
  OuterRadius = 34.5
  Placement = pos=(0,166.76,0) rot=(1,0,0;1.5708rad)
FEATURE [Part::Compound] Compound014
  Links = -> [Tube006,Cut008]
  Placement = pos=(0,0,0) rot=(0,0,1;4.71239rad)
FEATURE [Part::Cylinder] Cylinder015  label="Zylinder015"
  Angle = 360
  AttacherType = Attacher::AttachEngine3D
  FirstAngle = 0
  Height = 20
  Placement = pos=(0,179.75,0) rot=(1,0,0;1.5708rad)
  Radius = 22.25
  SecondAngle = 0
FEATURE [Part::Feature] Solid007  label="Hositrad_CF35-Blank007"
  Placement = pos=(0,166.75,0) rot=(0,0,1;0rad)
  shape: bbox 70 x 12.7 x 70 mm, 58 faces (baked)
FEATURE [Part::Cut] Cut009
  Base = -> Solid007
  Tool = -> Cylinder015
FEATURE [Part::FeaturePython] Tube007  # WARN: FeaturePython — macro-defined, semantics opaque (R4)
  AttacherType = Attacher::AttachEngine3D
  Height = 6
  InnerRadius = 22.25
  OuterRadius = 34.5
  Placement = pos=(0,166.76,0) rot=(1,0,0;1.5708rad)
FEATURE [Part::Compound] Compound015
  Links = -> [Tube007,Cut009]
  Placement = pos=(0,0,0) rot=(0,0,1;5.49779rad)
FEATURE [Part::Compound] Compound016
  Links = -> [Compound008,Compound009,Compound010,Compound011,Compound012,Compound013,Compound014,Compound015]
FEATURE [Part::Compound] Compound017
  Links = -> [Cut001,Compound016]
---- part parabolic_base.FCStd = doc fcstd_e95622d1a48c ----
FCSTD DOCUMENT  (FreeCAD 0.20R)
Label: parabolic_base
License: All rights reserved
LicenseURL: http://en.wikipedia.org/wiki/All_rights_reserved
objects: Part::Box×3, Part::Cylinder×2, Spreadsheet::Sheet×1, Sketcher::SketchObject×1, PartDesign::Revolution×1, PartDesign::Body×1, Part::MultiFuse×1, Part::Cut×1, Part::MultiCommon×1
note: 12 computed .brp shape members not serialized (recipe doc carries the construction recipe); baked Part::Feature solids carry a one-line shape summary decoded from their .brp

FEATURE [Spreadsheet::Sheet] Spreadsheet  label="MirrorParameters"
  cells = A1=Design parameters; E1=Calculated parameters; A2=Focal length; B2(focal_length)=0.75; C2=Focal length of the mirror; E2=Parabola section length; F2(parabola_section_length_uncut)==(max_width / 2 + zpos_correction) ^ 2 / (4 * focal_length); G2=Length of the parabola section (when maximum height matches maximum width); A3=Solid body length; B3(tot_length)=7; C3=Length of the solid starting at the parabola vertex; E3=Offset width to height; F3(height_to_width_offset)==-1 / (4 * focal_length) * (max_width / 2 + zpos_correction) ^ 2 + focal_length + center_offset; G3=Difference of maximum height and maximum width position along x axis by cutting on top; A4=Maximum height; B4(max_height)=1.7; C4=Maximum height (y axis) of the mirror. The mirror gets cut at this maximum; E4=Remaining material at beamhole; F4==parabola_section_length_uncut - focal_length - center_offset - beamhole_diameter / 2; G4=Width of the remaining material at the beamhole; A5=Maximum width; B5(max_width)=4.37; C5=Maximum width (diameter) of the mirror; E5=Height to width difference; F5==max_width / 2 - max_height; G5=The thickness of the material removed on top; A6=Center offset; B6(center_offset)=0; C6=Offset between center of beamhole and focal point (Shifts the focal point w.r.t. beam hole towards holder structure); A7=Sample hole diameter; B7(sample_hole_diameter)=3.39; C7=Diameter of the sample hole in the sample holder itself; A8=Beamhole diameter; B8(beamhole_diameter)=0.3; C8=Diameter for beamhole (has to match one of the drills); A9=Step height; B9(step_height)=0.18; C9=Height of the step to align with an alignment feature on the holder; A10=Z Positon correction / Offset (downwards) ; B10(zpos_correction)=0.45; C10=Shifts the mirror vertex by this correction downwards (without affecting the step); A12=Note: Do not forget to recalculate the Revolution/Sketch object after changing parameters or it will only affect the part!
FEATURE [Sketcher::SketchObject] Sketch  label="ParabolicSketch"
  FullyConstrained = false
  MapMode = 5
  Support = -> [XY_Plane001]
  expr: .Constraints.BodyLength = <<MirrorParameters>>.tot_length
  expr: .Constraints.CenterOffset = <<MirrorParameters>>.center_offset
  expr: .Constraints.FocalLength = <<MirrorParameters>>.focal_length
  expr: Constraints[9] = <<MirrorParameters>>.max_width / 2 + <<MirrorParameters>>.zpos_correction
  sketch-geometry (8):
    g0: GeomPoint X=0 Y=0 Z=0
    g1: GeomPoint X=0.75 Y=0 Z=0
    g2: LineSegment StartX=0.75 StartY=0 StartZ=0 EndX=7.75 EndY=0 EndZ=0
    g3: LineSegment StartX=7.75 StartY=0 StartZ=0 EndX=7.75 EndY=2.635 EndZ=0
    g4: ArcOfParabola CenterX=0.75 CenterY=0 CenterZ=0 NormalX=0 NormalY=0 NormalZ=1 Focal=0.75 AngleXU=3.14159 StartAngle=-2.635 EndAngle=0
    g5: GeomPoint X=0 Y=0 Z=0
    g6: LineSegment StartX=0.75 StartY=0 StartZ=0 EndX=0 EndY=0 EndZ=0
    g7: LineSegment StartX=-1.56441 StartY=2.635 StartZ=0 EndX=7.75 EndY=2.635 EndZ=0
  constraints (17):
    c: PointOnObject(g0,g-1)
    c: PointOnObject(g1,g-1)
    c: DistanceX(g-1,g0) = 0  'CenterOffset'
    c: DistanceX(g0,g1) = 0.75  'FocalLength'
    c: Coincident(g2,g1)
    c: PointOnObject(g2,g-1)
    c: Coincident(g3,g2)
    c: Vertical(g3)
    c: DistanceX(g2,g2) = 7  'BodyLength'
    c: DistanceY(g2,g3) = 2.635
    c: InternalAlignment(g5,g4)
    c: Coincident(g5,g0)
    c: Coincident(g4,g2)
    c: Coincident(g4,g2)
    c: Coincident(g7,g4)
    c: Coincident(g7,g3)
    c: Horizontal(g7)
FEATURE [PartDesign::Revolution] Revolution
  Angle = 180
  Axis = (1,0,0)
  Base = (0,0,0)
  Profile = -> Sketch
  ReferenceAxis = -> X_Axis001
FEATURE [PartDesign::Body] Body001  label="ParabolicBaseMirror"
  Group = -> [Sketch,Revolution]
  Origin = -> Origin001
  Placement = pos=(0,0,-0.45) rot=(0,0,1;0rad)
  Tip = -> Revolution
  expr: .Placement.Base.z = -<<MirrorParameters>>.zpos_correction
FEATURE [Part::Box] Box  label="UpperEdgeCuttingTool"
  AttacherType = Attacher::AttachEngine3D
  Height = 0.935
  Length = 9.31441
  Placement = pos=(-1.56441,-2.185,1.7) rot=(0,0,1;0rad)
  Width = 4.37
  expr: .Placement.Base.x = -1 * (<<MirrorParameters>>.parabola_section_length_uncut + <<MirrorParameters>>.tot_length - <<MirrorParameters>>.center_offset - <<MirrorParameters>>.focal_length - <<MirrorParameters>>.tot_length)
  expr: .Placement.Base.y = <<MirrorParameters>>.max_width / -2
  expr: .Placement.Base.z = <<MirrorParameters>>.max_height
  expr: Height = <<MirrorParameters>>.max_width / 2 - <<MirrorParameters>>.max_height + <<MirrorParameters>>.zpos_correction
  expr: Length = <<MirrorParameters>>.parabola_section_length_uncut + <<MirrorParameters>>.tot_length
  expr: Width = <<MirrorParameters>>.max_width
FEATURE [Part::Box] Box001  label="LowerStepCuttingTool"
  AttacherType = Attacher::AttachEngine3D
  Height = 0.63
  Length = 3.25941
  Placement = pos=(-1.56441,-2.185,-0.45) rot=(0,0,1;0rad)
  Width = 4.37
  expr: .Placement.Base.x = <<MirrorParameters>>.focal_length + <<MirrorParameters>>.center_offset - <<MirrorParameters>>.parabola_section_length_uncut
  expr: .Placement.Base.y = -<<MirrorParameters>>.max_width / 2
  expr: .Placement.Base.z = -<<MirrorParameters>>.zpos_correction
  expr: Height = <<MirrorParameters>>.step_height + <<MirrorParameters>>.zpos_correction
  expr: Length = <<MirrorParameters>>.sample_hole_diameter / 2 - <<MirrorParameters>>.height_to_width_offset
  expr: Width = <<MirrorParameters>>.max_width
FEATURE [Part::Cylinder] Cylinder  label="BeamholeCuttingTool"
  Angle = 360
  AttacherType = Attacher::AttachEngine3D
  FirstAngle = 0
  Height = 2.185
  Radius = 0.15
  SecondAngle = 0
  expr: .Placement.Base.x = -<<MirrorParameters>>.center_offset
  expr: Height = <<MirrorParameters>>.max_width / 2
  expr: Radius = <<MirrorParameters>>.beamhole_diameter / 2
FEATURE [Part::Box] Box002  label="ZPosCorrectionCuttingTool"
  AttacherType = Attacher::AttachEngine3D
  Height = 0.55
  Length = 9.31441
  Placement = pos=(-1.56441,-2.185,-0.55) rot=(0,0,1;0rad)
  Width = 4.37
  expr: .Placement.Base.x = -1 * (<<MirrorParameters>>.parabola_section_length_uncut + <<MirrorParameters>>.tot_length - <<MirrorParameters>>.center_offset - <<MirrorParameters>>.focal_length - <<MirrorParameters>>.tot_length)
  expr: .Placement.Base.y = <<MirrorParameters>>.max_width / -2
  expr: .Placement.Base.z = -<<MirrorParameters>>.zpos_correction - 0.1
  expr: Height = <<MirrorParameters>>.zpos_correction + 0.1
  expr: Length = <<MirrorParameters>>.parabola_section_length_uncut + <<MirrorParameters>>.tot_length
  expr: Width = <<MirrorParameters>>.max_width
FEATURE [Part::MultiFuse] Fusion  label="CuttingTools"
  Shapes = -> [Cylinder,Box,Box001,Box002]
FEATURE [Part::Cut] Cut  label="MirrorWithoutMount_NoLimit"
  Base = -> Body001
  Tool = -> Fusion
FEATURE [Part::Cylinder] Cylinder001  label="VolumeLimit"
  Angle = 360
  AttacherType = Attacher::AttachEngine3D
  FirstAngle = 0
  Height = 9.31441
  Placement = pos=(-1.56441,0,0) rot=(0,1,0;1.5708rad)
  Radius = 2.185
  SecondAngle = 0
  expr: .Placement.Base.x = <<MirrorParameters>>.focal_length + <<MirrorParameters>>.center_offset - <<MirrorParameters>>.parabola_section_length_uncut
  expr: Height = <<MirrorParameters>>.tot_length + <<MirrorParameters>>.parabola_section_length_uncut
  expr: Radius = <<MirrorParameters>>.max_width / 2
FEATURE [Part::MultiCommon] Common  label="MirrorWithoutMount"
  Shapes = -> [Cut,Cylinder001]
---- part parabolic_screwmount.FCStd = doc fcstd_0ac91f85fa90 ----
FCSTD DOCUMENT  (FreeCAD 0.19R24267 +99 (Git))
Label: parabolic_screwmount
License: All rights reserved
LicenseURL: http://en.wikipedia.org/wiki/All_rights_reserved
objects: Part::Cylinder×4, Part::Box×2, App::Link×1, Spreadsheet::Sheet×1, Part::Compound×1, Part::MultiFuse×1, Part::Cut×1
note: 9 computed .brp shape members not serialized (recipe doc carries the construction recipe); baked Part::Feature solids carry a one-line shape summary decoded from their .brp
EXTERNAL_REF file=parabolic_base.FCStd obj=Common
EXTERNAL_REF file=parabolic_base.FCStd obj=Spreadsheet

FEATURE [App::Link] Link  label="MirrorWithoutMount_Solid"
  LinkedObject = -> <external parabolic_base.FCStd>#Common
FEATURE [Spreadsheet::Sheet] Spreadsheet  label="ScrewMountParameters"
  cells = A1=Settings; E1=Importet properties (don't change here!); A2=Screw type; B2=M1; C2=Informative only (not updating below values); E2=Body offset; F2(body_offset)==<<parabolic_base>>#<<MirrorParameters>>.center_offset + <<parabolic_base>>#<<MirrorParameters>>.focal_length; G2=From parabolic_base: Offset of the body part with relation to Origin at the beamhole; A3=Through hole diameter; B3(mountscrew_through_dia)=1.2; C3=Close or medium fit diameter; E3=Body length; F3(body_length)==<<parabolic_base>>#<<MirrorParameters>>.tot_length; G3=From parabolic_base: Length of the body part; A4=Minimum material thickness; B4(min_material_thickness)=0.5; C4=Leave at least this amount of material if possible; E4=Body diameter; F4(body_width)==<<parabolic_base>>#<<MirrorParameters>>.max_width; G4=From parabolic_base: Diameter of body (max. width); A5=Screw head diameter; B5(screwhead_dia)=2; C5=Diameter of screw head; E5=Body height; F5(body_height)==<<parabolic_base>>#<<MirrorParameters>>.max_height; G5=From parabolic_base: Height of body (max body); A6=Screw head height max; B6(screwhead_height_max)==sqrt((body_width / 2) ^ 2 - (screwhead_dia / 2) ^ 2) - min_material_thickness; C6=Absolute maximum that leaves minimum material intact; A7=Screw head height real; B7(screwhead_height)=0.7; C7=Height of screw head; A8=Remaining material below screw head; B8(calculated_remaining_below_screwhead)==sqrt((body_width / 2) ^ 2 - (screwhead_dia / 2) ^ 2) - screwhead_height; C8=Remaining material below head of screw; A9=Remaining material on side of screw head; B9==(body_width - screwhead_dia) / 2; C9=Remaining material on both sides of the screw head; A10=Remaining material on side of screw; B10==(body_width - mountscrew_through_dia) / 2; C10=Remaining material on both sides of the screw
FEATURE [Part::Box] Box  label="CuttingToolThroughHole"
  AttacherType = Attacher::AttachEngine3D
  Height = 1.7
  Length = 4
  Placement = pos=(2.25,-0.6,0) rot=(0,0,1;0rad)
  Width = 1.2
  expr: Width = <<ScrewMountParameters>>.mountscrew_through_dia
  expr: Length = <<ScrewMountParameters>>.body_length - 2 * <<ScrewMountParameters>>.min_material_thickness - <<ScrewMountParameters>>.screwhead_dia
  expr: Height = <<ScrewMountParameters>>.body_height
  expr: .Placement.Base.y = -<<ScrewMountParameters>>.mountscrew_through_dia / 2
  expr: .Placement.Base.x = <<ScrewMountParameters>>.body_offset + <<ScrewMountParameters>>.min_material_thickness + <<ScrewMountParameters>>.screwhead_dia / 2
FEATURE [Part::Box] Box001  label="CuttingToolScrewHead"
  AttacherType = Attacher::AttachEngine3D
  Height = 0.942264
  Length = 4
  Placement = pos=(2.25,-1,1.24274) rot=(0,0,1;0rad)
  Width = 2
  expr: Width = <<ScrewMountParameters>>.screwhead_dia
  expr: Length = <<ScrewMountParameters>>.body_length - 2 * <<ScrewMountParameters>>.min_material_thickness - <<ScrewMountParameters>>.screwhead_dia
  expr: Height = <<ScrewMountParameters>>.body_width / 2 - <<ScrewMountParameters>>.calculated_remaining_below_screwhead
  expr: .Placement.Base.z = <<ScrewMountParameters>>.calculated_remaining_below_screwhead
  expr: .Placement.Base.y = -<<ScrewMountParameters>>.screwhead_dia / 2
  expr: .Placement.Base.x = <<ScrewMountParameters>>.body_offset + <<ScrewMountParameters>>.min_material_thickness + <<ScrewMountParameters>>.screwhead_dia / 2
FEATURE [Part::Compound] Compound
  Links = -> [Link]
FEATURE [Part::Cylinder] Cylinder  label="HeadFront"
  Angle = 360
  AttacherType = Attacher::AttachEngine3D
  Height = 10
  Placement = pos=(2.25,0,1.24274) rot=(0,0,1;0rad)
  Radius = 1
  expr: .Placement.Base.x = <<ScrewMountParameters>>.body_offset + <<ScrewMountParameters>>.min_material_thickness + <<ScrewMountParameters>>.screwhead_dia / 2
  expr: .Placement.Base.z = <<ScrewMountParameters>>.calculated_remaining_below_screwhead
  expr: Radius = <<ScrewMountParameters>>.screwhead_dia / 2
FEATURE [Part::Cylinder] Cylinder001  label="HeadBack"
  Angle = 360
  AttacherType = Attacher::AttachEngine3D
  Height = 10
  Placement = pos=(6.25,0,1.24274) rot=(0,0,1;0rad)
  Radius = 1
  expr: Radius = <<ScrewMountParameters>>.screwhead_dia / 2
  expr: .Placement.Base.z = <<ScrewMountParameters>>.calculated_remaining_below_screwhead
  expr: .Placement.Base.x = <<ScrewMountParameters>>.body_offset + <<ScrewMountParameters>>.min_material_thickness + <<ScrewMountParameters>>.screwhead_dia / 2 + <<ScrewMountParameters>>.body_length - 2 * <<ScrewMountParameters>>.min_material_thickness - <<ScrewMountParameters>>.screwhead_dia
FEATURE [Part::Cylinder] Cylinder002  label="ScrewThroughFront"
  Angle = 360
  AttacherType = Attacher::AttachEngine3D
  Height = 10
  Placement = pos=(2.25,0,0) rot=(0,0,1;0rad)
  Radius = 0.6
  expr: .Placement.Base.y = 0
  expr: Radius = <<ScrewMountParameters>>.mountscrew_through_dia / 2
  expr: .Placement.Base.x = <<ScrewMountParameters>>.body_offset + <<ScrewMountParameters>>.min_material_thickness + <<ScrewMountParameters>>.screwhead_dia / 2
FEATURE [Part::Cylinder] Cylinder003  label="ScrewThroughBack"
  Angle = 360
  AttacherType = Attacher::AttachEngine3D
  Height = 10
  Placement = pos=(6.25,0,0) rot=(0,0,1;0rad)
  Radius = 0.6
  expr: .Placement.Base.x = <<ScrewMountParameters>>.body_offset + <<ScrewMountParameters>>.min_material_thickness + <<ScrewMountParameters>>.screwhead_dia / 2 + <<ScrewMountParameters>>.body_length - 2 * <<ScrewMountParameters>>.min_material_thickness - <<ScrewMountParameters>>.screwhead_dia
  expr: Radius = <<ScrewMountParameters>>.mountscrew_through_dia / 2
FEATURE [Part::MultiFuse] Fusion  label="CuttingTools"
  Shapes = -> [Box001,Box,Cylinder,Cylinder001,Cylinder002,Cylinder003]
FEATURE [Part::Cut] Cut  label="ParabolicMirrorWithScrewmount"
  Base = -> Compound
  Tool = -> Fusion
